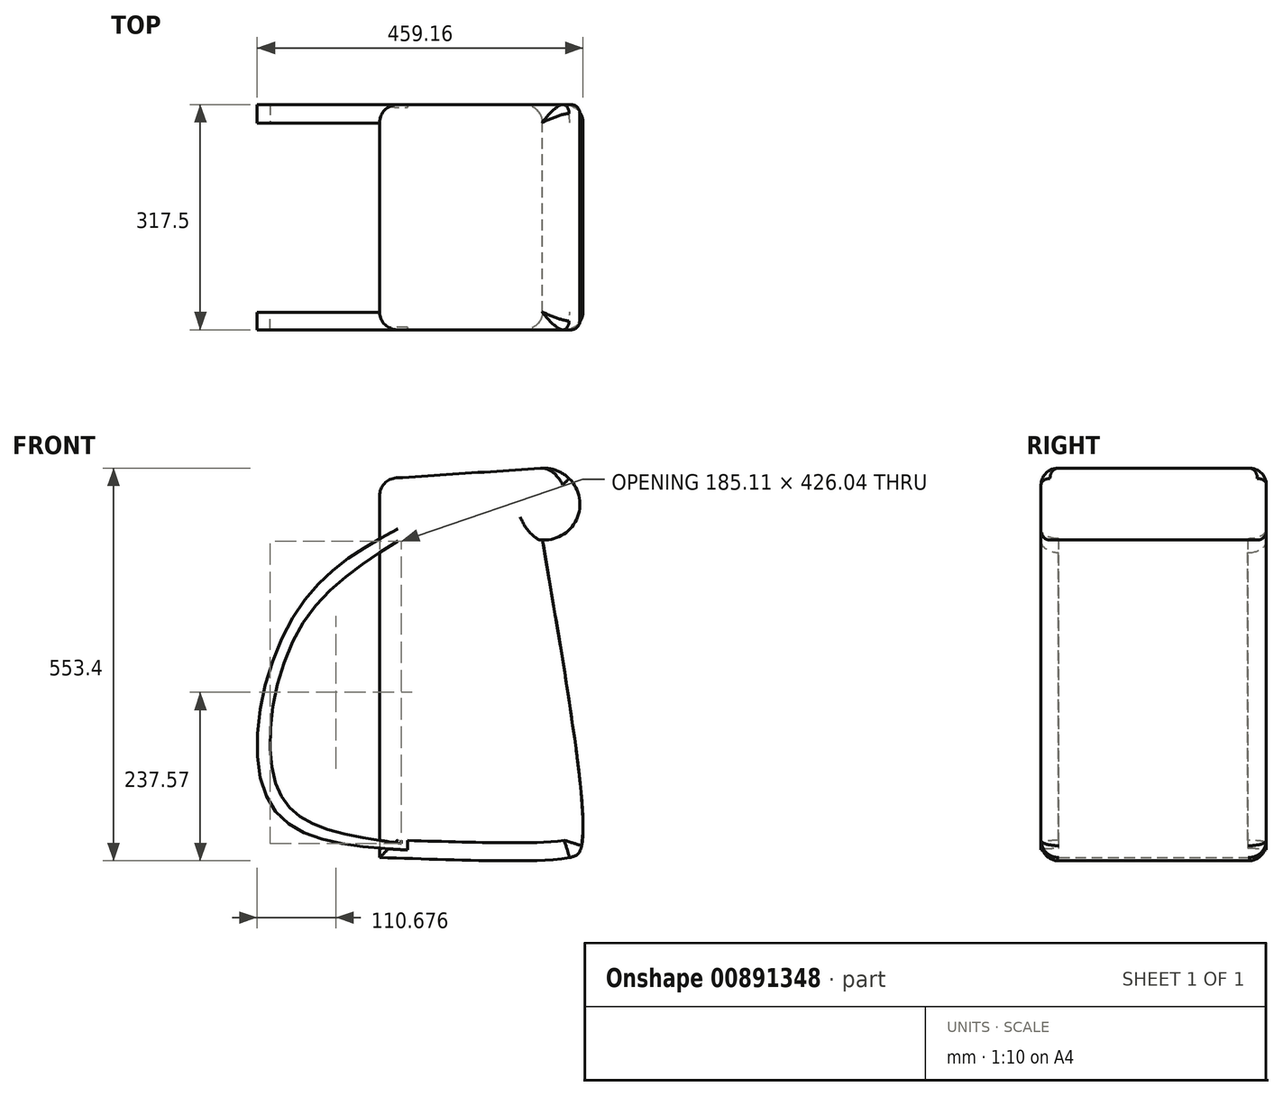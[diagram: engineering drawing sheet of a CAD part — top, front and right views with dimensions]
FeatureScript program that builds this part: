
annotation { "Feature Type Name" : "Feature", "Feature Type Description" : "" }
export const myFeature = defineFeature(function(context is Context, id is Id, definition is map)
    precondition{}
    {
        {
            var Q0;
            Q0=qCreatedBy(makeId("Front.planeOp"),FACE);
            var sketch = newSketch(context, id + "F0", { "sketchPlane" : qUnion([Q0])});
            skLineSegment(sketch, "E0", {"start": v(0, 0) * mm, "end": v(0, 533.4) * mm});
            skFitSpline(sketch, "E1", {"points": [v(0, 0) * mm, v(268.72, 0) * mm, v(283.22, 11.39) * mm, v(284.12, 89.32) * mm, v(228.85, 451.79) * mm], "startDerivative": vector(1043.75, -36.53) * mm, "endDerivative": vector(-181.52, 1063.46) * mm});
            skArc(sketch, "E2", {"start": v(229.6, 447.39) * mm, "mid": v(282.2, 499.44) * mm, "end": v(226.74, 548.43) * mm});
            skFitSpline(sketch, "E3", {"points": [v(0, 533.4) * mm, v(229.64, 548.62) * mm], "startDerivative": vector(229.63, 15.35) * mm, "endDerivative": vector(229.63, 15.35) * mm});
            skSolve(sketch);
        }
        {
            var Q0;
            {var subQ1=sQuery(id+"F0.wireOp",EDGE,"E0");Q0=makeQuery(id+"F0.imprint","IMPRINT",FACE,{"disambiguationData":[TD([[makeQuery(id+"F0.imprint","IMPRINT",EDGE,{"derivedFrom":subQ1}),-1.0]])]});}
            extrude(context, id + "F1", {"entities" : qUnion([Q0]), "depth" : 317.5 * mm, "offsetDistance" : 25.4 * mm});
        }
        {
            var Q0;
            Q0=makeQuery(id+"F1.opExtrude","CAP_EDGE",EDGE,{"disambiguationData":[OSD([sQuery(id+"F0.wireOp",EDGE,"E1")])],"isStart":false});
            var Q1;
            Q1=makeQuery(id+"F1.opExtrude","CAP_EDGE",EDGE,{"disambiguationData":[OSD([sQuery(id+"F0.wireOp",EDGE,"E1")])],"isStart":true});
            var Q2;
            Q2=makeQuery(id+"F1.opExtrude","CAP_EDGE",EDGE,{"disambiguationData":[OSD([sQuery(id+"F0.wireOp",EDGE,"E3")])],"isStart":false});
            var Q3;
            Q3=makeQuery(id+"F1.opExtrude","CAP_EDGE",EDGE,{"disambiguationData":[OSD([sQuery(id+"F0.wireOp",EDGE,"E3")])],"isStart":true});
            var Q4;
            Q4=makeQuery(id+"F1.opExtrude","SWEPT_FACE",FACE,{"disambiguationData":[OSD([sQuery(id+"F0.wireOp",EDGE,"E3")])]});
            var Q5;
            Q5=makeQuery(id+"F1.opExtrude","CAP_EDGE",EDGE,{"disambiguationData":[OSD([sQuery(id+"F0.wireOp",EDGE,"E0")])],"isStart":false});
            var Q6;
            Q6=makeQuery(id+"F1.opExtrude","CAP_EDGE",EDGE,{"disambiguationData":[OSD([sQuery(id+"F0.wireOp",EDGE,"E0")])],"isStart":true});
            fillet(context, id + "F2", {"entities" : qUnion([Q0, Q1, Q2, Q3, Q4, Q5, Q6]), "radius" : 25.4 * mm, "tangentPropagation" : true, "allowEdgeOverflow" : false});
        }
        {
            var Q0;
            Q0=qCreatedBy(makeId("Front.planeOp"),FACE);
            var sketch = newSketch(context, id + "F3", { "sketchPlane" : qUnion([Q0])});
            skFitSpline(sketch, "E4", {"points": [v(39.34, 470.49) * mm, v(-122.52, 337.7) * mm, v(-152.98, 73.7) * mm, v(39.34, 10.44) * mm], "startDerivative": vector(-562.7, -297.36) * mm, "endDerivative": vector(753.97, -46.55) * mm});
            skFitSpline(sketch, "E5", {"points": [v(39.34, 470.49) * mm, v(39.34, 10.44) * mm], "startDerivative": vector(0, -460.05) * mm, "endDerivative": vector(0, -460.05) * mm});
            skFitSpline(sketch, "E6", {"points": [v(30.75, 19.8) * mm, v(-105.15, 53.4) * mm, v(-152.02, 128.38) * mm, v(-112.18, 323.65) * mm, v(32.32, 450.18) * mm], "startDerivative": vector(-640.56, 87.68) * mm, "endDerivative": vector(587.3, 367.44) * mm});
            skLineSegment(sketch, "E7", {"start": v(30.75, 19.8) * mm, "end": v(32.32, 450.18) * mm});
            skSolve(sketch);
        }
        {
            var Q0;
            Q0 = qSketchRegion(id + "F3", true);
            extrude(context, id + "F4", {"entities" : qUnion([Q0]), "operationType" : NewBodyOperationType.ADD, "depth" : 317.5 * mm, "offsetDistance" : 25.4 * mm});
        }
        {
            var Q0;
            Q0=qCreatedBy(makeId("Top.planeOp"),FACE);
            var sketch = newSketch(context, id + "F5", { "sketchPlane" : qUnion([Q0])});
            skLineSegment(sketch, "E8.bottom", {"start": v(0, -292.79) * mm, "end": v(-190.45, -292.79) * mm});
            skLineSegment(sketch, "E8.top", {"start": v(0, -26.34) * mm, "end": v(-190.45, -26.34) * mm});
            skLineSegment(sketch, "E8.left", {"start": v(0, -292.79) * mm, "end": v(0, -26.34) * mm});
            skLineSegment(sketch, "E8.right", {"start": v(-190.45, -292.79) * mm, "end": v(-190.45, -26.34) * mm});
            skSolve(sketch);
        }
        {
            var Q0;
            Q0 = qSketchRegion(id + "F5", true);
            extrude(context, id + "F6", {"entities" : qUnion([Q0]), "operationType" : NewBodyOperationType.REMOVE, "depth" : 609.6 * mm, "offsetDistance" : 25.4 * mm});
        }
        {
            var Q0;
            Q0=makeQuery(id+"F1.opExtrude","CAP_EDGE",EDGE,{"disambiguationData":[OSD([sQuery(id+"F0.wireOp",EDGE,"E2")])],"isStart":true});
            var Q1;
            Q1=makeQuery(id+"F1.opExtrude","CAP_EDGE",EDGE,{"disambiguationData":[OSD([sQuery(id+"F0.wireOp",EDGE,"E2")])],"isStart":false});
            fillet(context, id + "F7", {"entities" : qUnion([Q0, Q1]), "radius" : 12.7 * mm, "tangentPropagation" : true, "allowEdgeOverflow" : false});
        }
    });
